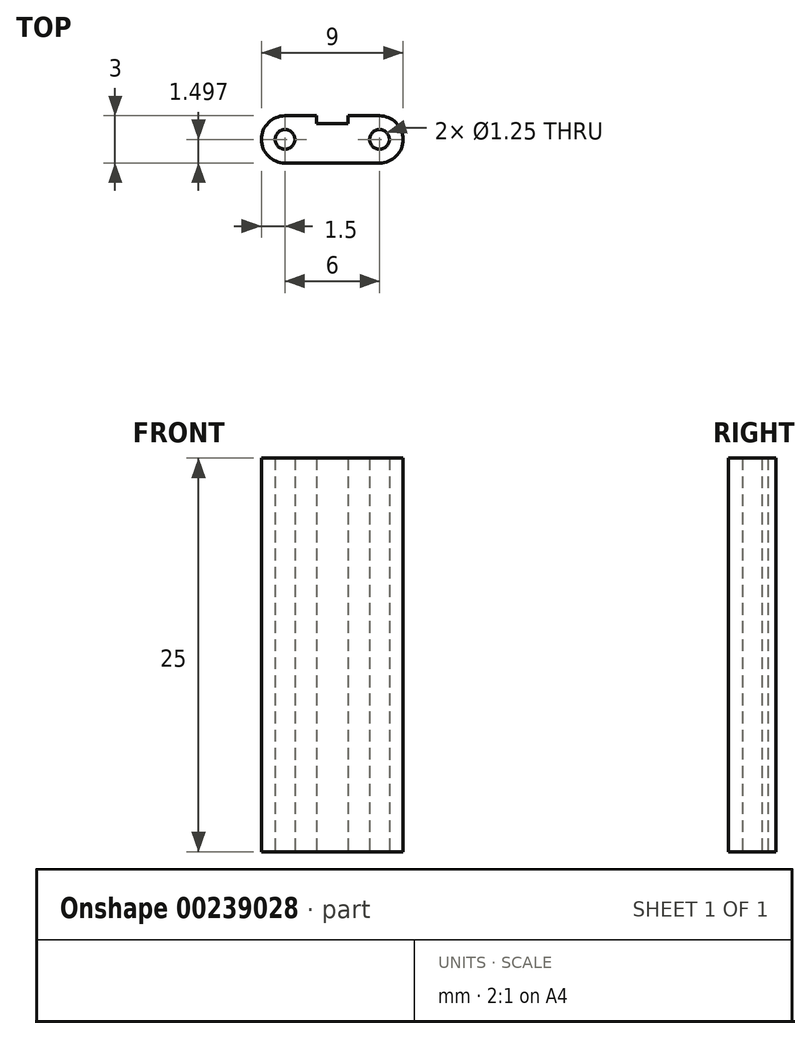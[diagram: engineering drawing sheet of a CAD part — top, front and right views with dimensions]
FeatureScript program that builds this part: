
annotation { "Feature Type Name" : "Feature", "Feature Type Description" : "" }
export const myFeature = defineFeature(function(context is Context, id is Id, definition is map)
    precondition{}
    {
        {
            var Q0;
            Q0=qCreatedBy(makeId("Top.planeOp"),FACE);
            var sketch = newSketch(context, id + "F0", { "sketchPlane" : qUnion([Q0])});
            skLineSegment(sketch, "E0", {"start": v(-17.96, -22.86) * mm, "end": v(-11.96, -22.86) * mm});
            skPoint(sketch, "E1", {"position": v(-11.96, -21.36) * mm});
            skPoint(sketch, "E2", {"position": v(-11.96, -19.86) * mm});
            skPoint(sketch, "E3", {"position": v(-17.96, -21.36) * mm});
            skPoint(sketch, "E4", {"position": v(-17.96, -19.86) * mm});
            skLineSegment(sketch, "E5", {"start": v(-17.96, -19.86) * mm, "end": v(-15.96, -19.86) * mm});
            skLineSegment(sketch, "E6", {"start": v(-15.96, -19.86) * mm, "end": v(-15.96, -20.36) * mm});
            skLineSegment(sketch, "E7", {"start": v(-15.96, -20.36) * mm, "end": v(-13.96, -20.36) * mm});
            skLineSegment(sketch, "E8", {"start": v(-13.96, -20.36) * mm, "end": v(-13.96, -19.86) * mm});
            skLineSegment(sketch, "E9", {"start": v(-13.96, -19.86) * mm, "end": v(-11.96, -19.86) * mm});
            skCircle(sketch, "E10", {"center": v(-17.96, -21.36) * mm, "radius": 0.62 * mm});
            skCircle(sketch, "E11", {"center": v(-11.96, -21.36) * mm, "radius": 0.62 * mm});
            skArc(sketch, "E12", {"start": v(-17.96, -19.86) * mm, "mid": v(-19.46, -21.36) * mm, "end": v(-17.96, -22.86) * mm});
            skArc(sketch, "E13", {"start": v(-11.96, -22.86) * mm, "mid": v(-10.46, -21.36) * mm, "end": v(-11.96, -19.86) * mm});
            skSolve(sketch);
        }
        {
            var Q0;
            Q0=makeQuery(id+"F0.imprint","IMPRINT",FACE,{"disambiguationData":[TD([[makeQuery(id+"F0.imprint","IMPRINT",EDGE,{"derivedFrom":sQuery(id+"F0.wireOp",EDGE,"E0")}),1.0]])]});
            extrude(context, id + "F1", {"entities" : qUnion([Q0]), "depth" : 25 * mm});
        }
    });
